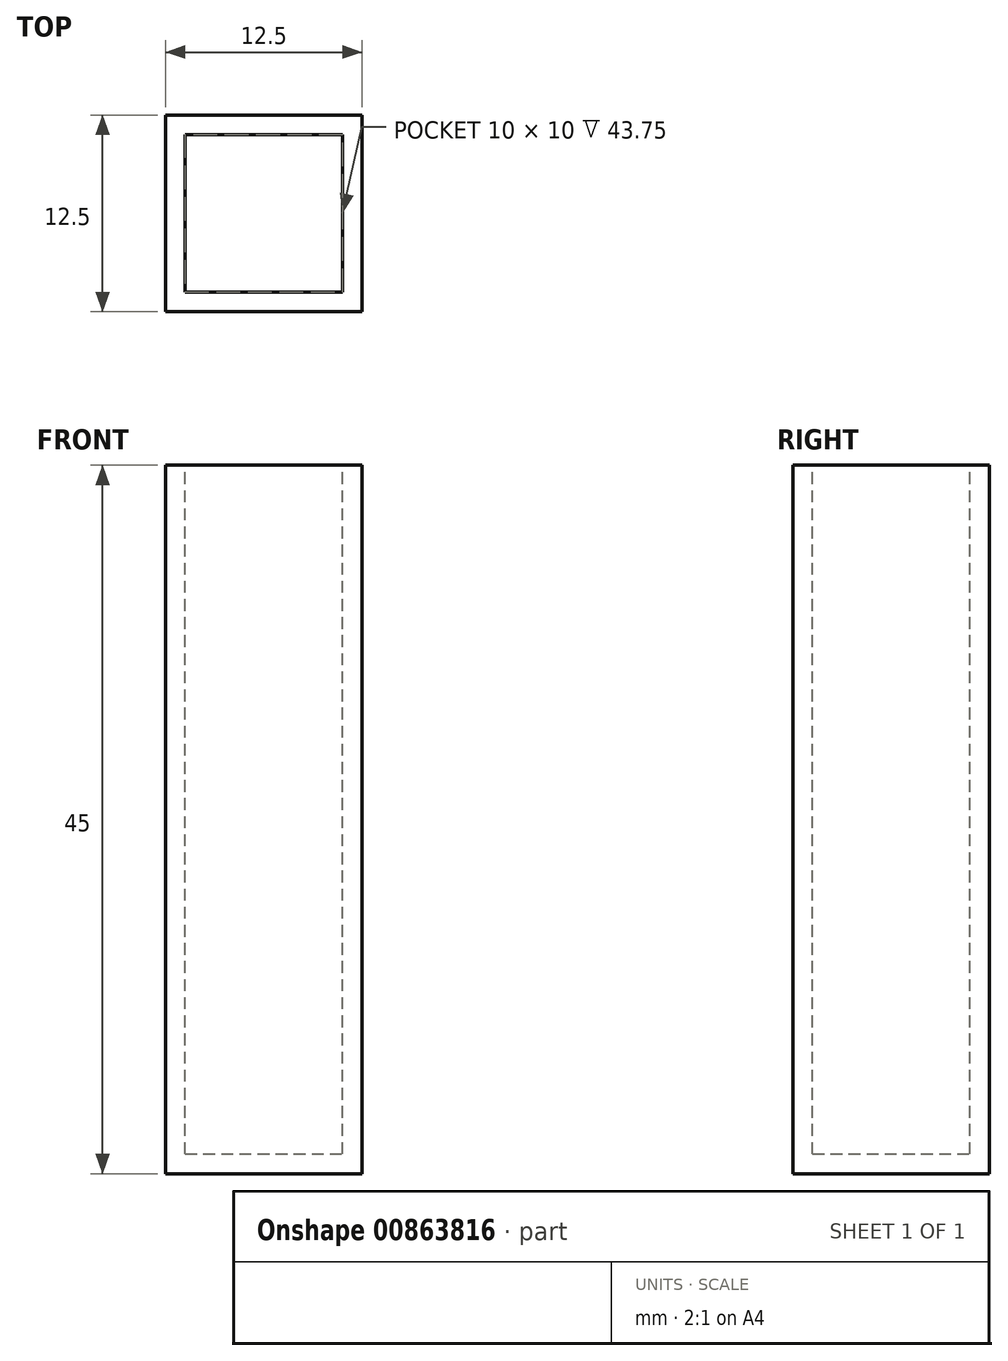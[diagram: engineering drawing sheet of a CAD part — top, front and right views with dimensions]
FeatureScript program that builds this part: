
annotation { "Feature Type Name" : "Feature", "Feature Type Description" : "" }
export const myFeature = defineFeature(function(context is Context, id is Id, definition is map)
    precondition{}
    {
        {
            var Q0;
            Q0=qCreatedBy(makeId("Front.planeOp"),FACE);
            var sketch = newSketch(context, id + "F0", { "sketchPlane" : qUnion([Q0])});
            skLineSegment(sketch, "E0.bottom", {"start": v(0, 0) * mm, "end": v(12.5, 0) * mm});
            skLineSegment(sketch, "E0.top", {"start": v(0, 45) * mm, "end": v(12.5, 45) * mm});
            skLineSegment(sketch, "E0.left", {"start": v(0, 0) * mm, "end": v(0, 45) * mm});
            skLineSegment(sketch, "E0.right", {"start": v(12.5, 0) * mm, "end": v(12.5, 45) * mm});
            skSolve(sketch);
        }
        {
            var Q0;
            Q0 = qSketchRegion(id + "F0", true);
            extrude(context, id + "F1", {"entities" : qUnion([Q0]), "depth" : 12.5 * mm, "offsetDistance" : 25 * mm});
        }
        {
            var Q0;
            Q0=makeQuery(id+"F1.opExtrude","SWEPT_FACE",FACE,{"disambiguationData":[OSD([sQuery(id+"F0.wireOp",EDGE,"E0.top")])]});
            shell(context, id + "F2", {"entities" : qUnion([Q0]), "thickness" : 1.25 * mm});
        }
    });
